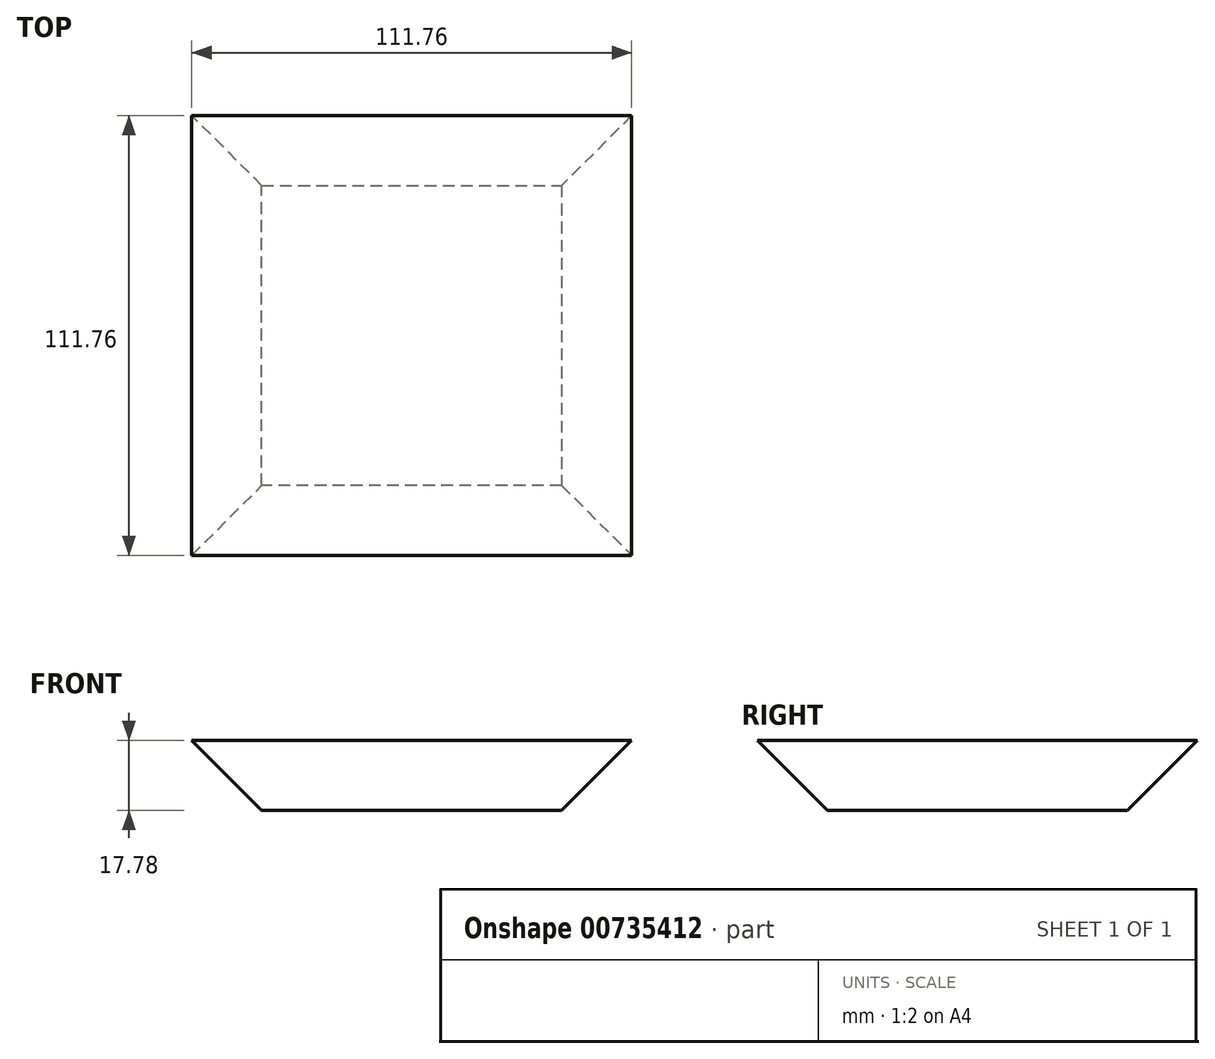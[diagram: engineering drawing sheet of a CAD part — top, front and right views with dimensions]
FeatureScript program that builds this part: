
annotation { "Feature Type Name" : "Feature", "Feature Type Description" : "" }
export const myFeature = defineFeature(function(context is Context, id is Id, definition is map)
    precondition{}
    {
        {
            var Q0;
            Q0=qCreatedBy(makeId("Top.planeOp"),FACE);
            var sketch = newSketch(context, id + "F0", { "sketchPlane" : qUnion([Q0])});
            skLineSegment(sketch, "E0.bottom", {"start": v(-38.1, 38.1) * mm, "end": v(38.1, 38.1) * mm});
            skLineSegment(sketch, "E0.top", {"start": v(-38.1, -38.1) * mm, "end": v(38.1, -38.1) * mm});
            skLineSegment(sketch, "E0.left", {"start": v(-38.1, 38.1) * mm, "end": v(-38.1, -38.1) * mm});
            skLineSegment(sketch, "E0.right", {"start": v(38.1, 38.1) * mm, "end": v(38.1, -38.1) * mm});
            skPoint(sketch, "E0.middle", {"position": v(0, 0) * mm});
            skSolve(sketch);
        }
        {
            var Q0;
            Q0=makeQuery(id+"F0.imprint","IMPRINT",FACE,{"disambiguationData":[TD([[makeQuery(id+"F0.imprint","IMPRINT",EDGE,{"derivedFrom":sQuery(id+"F0.wireOp",EDGE,"E0.bottom")}),-1.0]])]});
            extrude(context, id + "F1", {"entities" : qUnion([Q0]), "depth" : 17.78 * mm, "offsetDistance" : 25.4 * mm, "hasDraft" : true, "draftAngle" : 45 * degree});
        }
    });
